# Revit family: HVAC_Other_Enertech_CTC_EL-9-26
name_source: partatom
category: Specialty Equipment
revit_build: Autodesk Revit 2018 (Build: 20170223_1515(x64)
units: mm (PartAtom-declared; Revit-internal decimal feet)

## family parameters
Always vertical = No
Cut with Voids When Loaded = No
OmniClass Number = 23.75.00.00
OmniClass Title = Climate Control (HVAC)
Part Type = Normal
Room Calculation Point = No
Round Connector Dimension = Use Diameter
Shared = No
Work Plane-Based = No

## types (3) — shared parameters
AssetType = Fixed
BIMObjectName = HVAC_Other_Enertech_CTC_EL-9-26
Brand = CTC
Category = electrical heating
Color = white
DurationUnit = Year
EnergyClass_HotWater_TapProfile = A/XL
HasProtectiveEarth = Yes
IP_Code = IP44
IfcExportAs = IfcElectricalDeviceCommon
IfcExportType = HEATER
Manufacturer = Enertech AB
ManufacturerCountry = Sweden
ManufacturerName = Enertech AB
ManufacturerURL = https://ctc.se
Material = Steel
MaxOperatingPressureThermalStore = 7 bar
NBSDescription = Air to water heat pumps
NBSReference = 90-40-40/320
Name = CTC_EL-9-26
NominalCurrent = 0 A
NominalDepth = 138 mm
NominalFrequencyRange = 50 Hz
NominalHeight = 567 mm
NominalVoltage = 400 V
NominalWidth = 244 mm
PhaseAngle = 0.00°
PowerFactor = 0 W
PumpMainMaterial = Stainless Steel
PumpSecondaryMaterial = Brass
RatedVoltage = 1200 V
Shape = Rectangular
Size = 138x244x563 mm
SoundPowerLWA = 35 dB(A)
Touchscreen = No
UNSPSCCode = 40102003
URL = https://ctc-heating.com
Uniclass2 = Pr_40_70_65
Uniclass2015Description = Preparation catering equipment
Uniclass2015Reference = Pr_40_70_65
UsageCurrent = 0 A
Version = 1
VersionDate = 24/05/2022
WarrantyDurationUnit = Year
zero-valued in all types: Cost

## per-type parameters (varying)
| type | Description | EANNumber | ElectricalDeviceNominalPower | GroupFuse | Model | ModelNumber | OutputRangeIimmersionHeater | ProductInformation | RatedCurrent | WaterVolumeHeathingSystem | Weight |
| CTC EL 9 400V3N | A compact and easy-to-install electric flow heater with three power stages: 3, 6 and 9 kW. Often used as additional heat in heat pump systems | 7333077098377 | 9000 W | 16 A | CTC EL 9 | 589840001 | 3-9 kW | A compact and easy-to-install electric flow heater with three power stages: 3, 6 and 9 kW. Often used as additional heat in heat pump systems | 13 A | 1.6 liters | 9.3 kg |
| CTC EL 15 400V3N | A compact and easy-to-install electric flow heater with three power stages: 5, 10 and 15 kW. Often used as additional heat in heat pump systems | 7333077098384 | 15000 W | 25 A | CTC EL 15 | 589841001 | 5-15 kW | A compact and easy-to-install electric flow heater with three power stages: 5, 10 and 15 kW. Often used as additional heat in heat pump systems | 22 A | 4.5 liters | 11 kg |
| CTC EL 26 400V3N | A compact and easy-to-install electric flow heater with seven power stages: from 4 kW to 26 kW. Often used as additional heat in heat pump systems | 7333077098353 | 26000 W | 40 A | CTC EL 26 | 589842001 | 4-26 kW | A compact and easy-to-install electric flow heater with seven power stages: from 4 kW to 26 kW. Often used as additional heat in heat pump systems | 38 A | 4.5 liters | 15 kg |

## geometry (parser evidence)
native form markers: Sweep x4
no freeform markers — native parametric forms only
